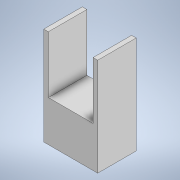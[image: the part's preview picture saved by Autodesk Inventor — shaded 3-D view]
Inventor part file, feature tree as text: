
AUTODESK INVENTOR PART (.ipt)
format: ipt  version: 2020 (Build 240168000, 168)  size: 130,048 bytes
history: native  units: mm
features: extrude x3, sketch x3
ambient origin geometry x8: Origin, YZ Plane, XZ Plane, XY Plane, X Axis, Y Axis, Z Axis, Center Point
bodies: Solid1 (feature_tree)
feature tree (6):
  extrude  "Extrusion1"  Depth=80.0mm
  extrude  "Extrusion2"  Depth=6.0mm
  extrude  "Extrusion4"  Depth=6.0mm
  sketch  "Sketch1"  dims[d0=70.0mm d1=80.0mm]
  sketch  "Sketch2"  dims[d2=80.0mm d3=6.0mm]
  sketch  "Sketch3"  dims[d4=50.0mm d5=0.0mm d7=6.0mm d8=40.0mm d9=0.0mm d15=70.0mm d16=7.0mm d17=50.0mm d18=0.0mm d6=0.5mm]
